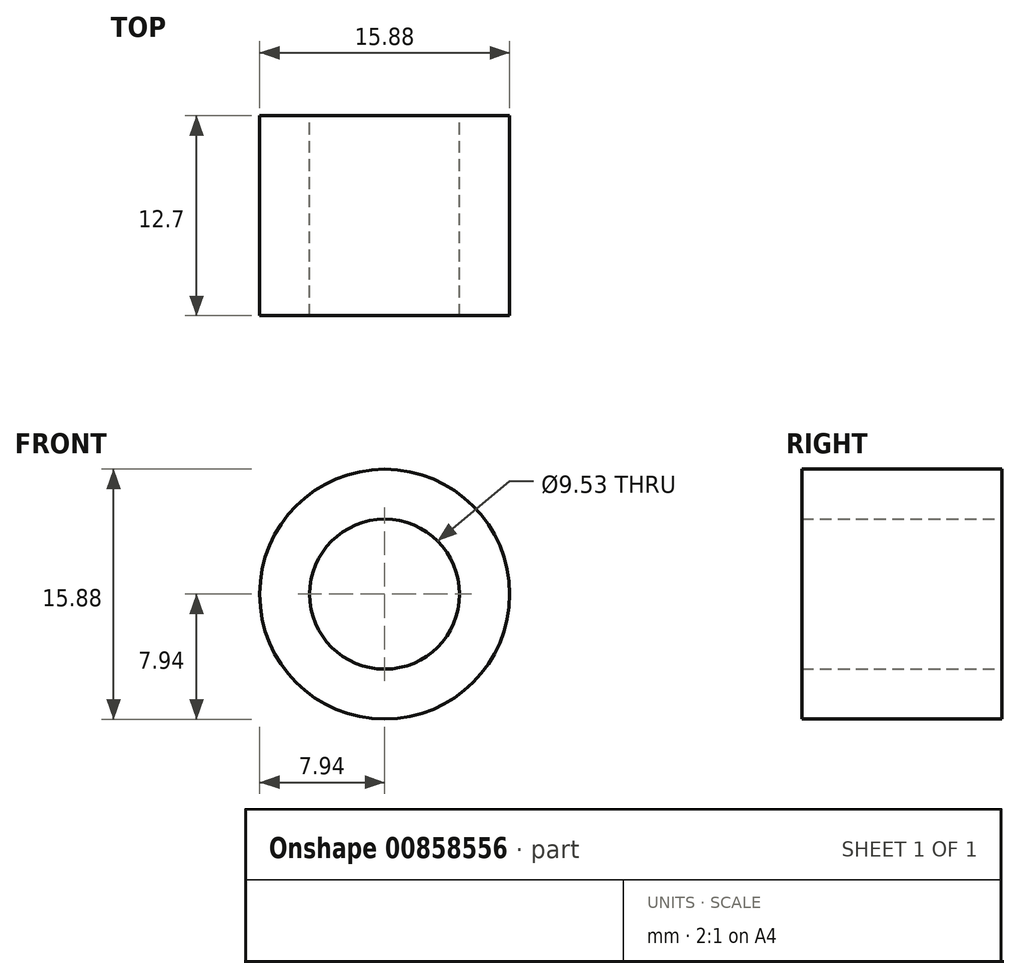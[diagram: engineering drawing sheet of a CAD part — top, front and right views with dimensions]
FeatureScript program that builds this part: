
annotation { "Feature Type Name" : "Feature", "Feature Type Description" : "" }
export const myFeature = defineFeature(function(context is Context, id is Id, definition is map)
    precondition{}
    {
        {
            var Q0;
            Q0=qCreatedBy(makeId("Front.planeOp"),FACE);
            var sketch = newSketch(context, id + "F0", { "sketchPlane" : qUnion([Q0])});
            skCircle(sketch, "E0", {"center": v(0, 0) * mm, "radius": 4.76 * mm});
            skCircle(sketch, "E1", {"center": v(0, 0) * mm, "radius": 7.94 * mm});
            skSolve(sketch);
        }
        {
            var Q0;
            Q0=makeQuery(id+"F0.imprint","IMPRINT",FACE,{"disambiguationData":[TD([[makeQuery(id+"F0.imprint","IMPRINT",EDGE,{"derivedFrom":sQuery(id+"F0.wireOp",EDGE,"E0")}),-1.0]])]});
            extrude(context, id + "F1", {"entities" : qUnion([Q0]), "depth" : 12.7 * mm, "offsetDistance" : 25.4 * mm});
        }
    });
